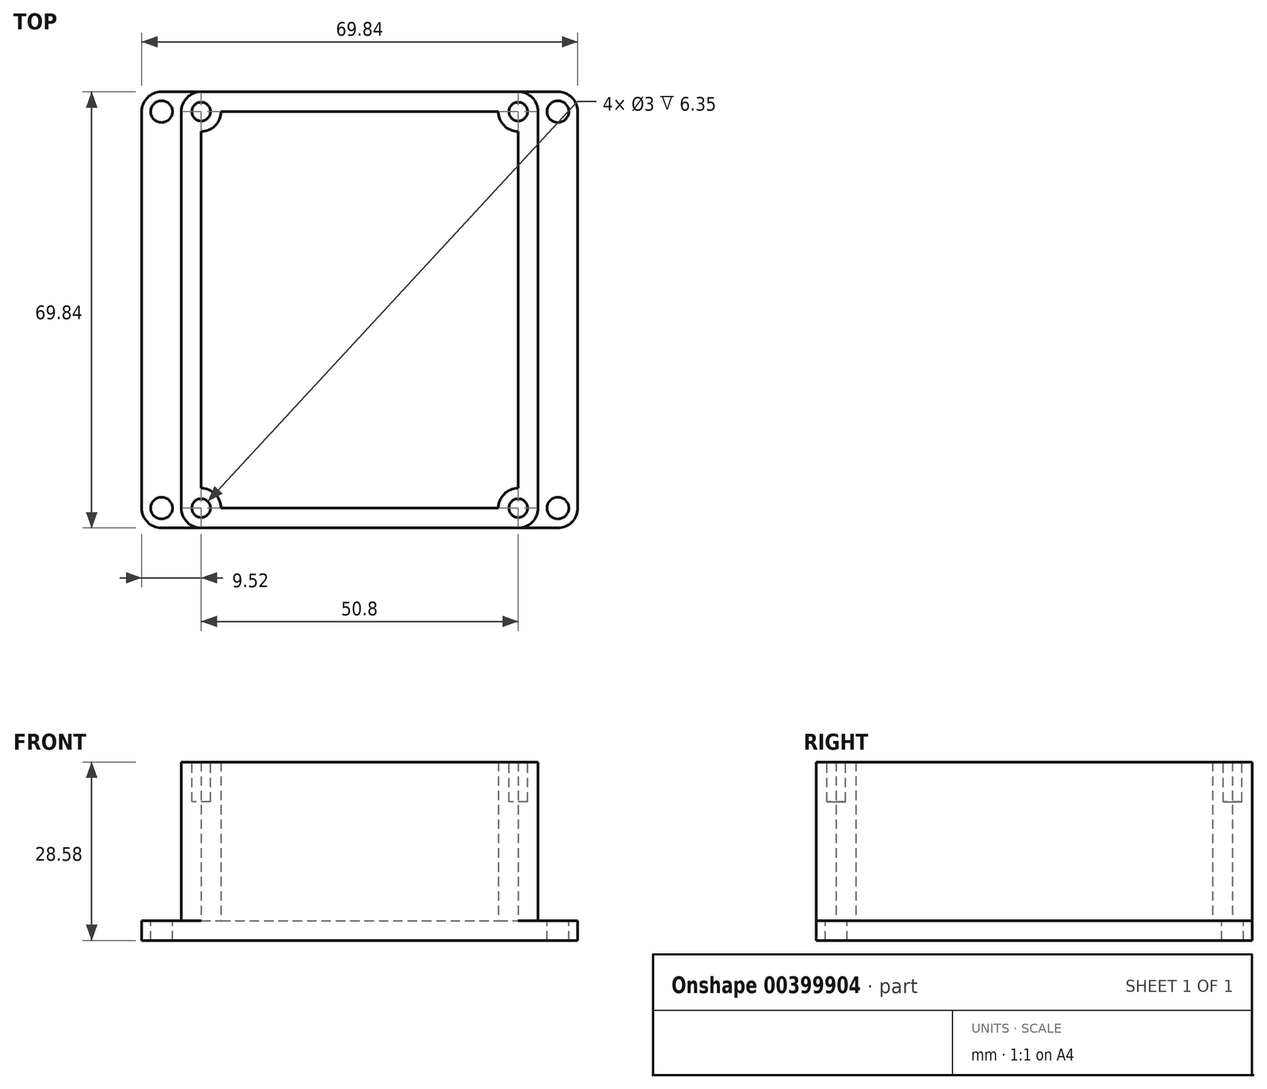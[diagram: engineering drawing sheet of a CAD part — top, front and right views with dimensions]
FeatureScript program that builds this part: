
annotation { "Feature Type Name" : "Feature", "Feature Type Description" : "" }
export const myFeature = defineFeature(function(context is Context, id is Id, definition is map)
    precondition{}
    {
        {
            var Q0;
            Q0=qCreatedBy(makeId("Top.planeOp"),FACE);
            var sketch = newSketch(context, id + "F0", { "sketchPlane" : qUnion([Q0])});
            skLineSegment(sketch, "E0.bottom", {"start": v(-34.93, 34.93) * mm, "end": v(34.93, 34.93) * mm});
            skLineSegment(sketch, "E0.top", {"start": v(-34.93, -34.93) * mm, "end": v(34.93, -34.93) * mm});
            skLineSegment(sketch, "E0.left", {"start": v(-34.93, 34.93) * mm, "end": v(-34.93, -34.93) * mm});
            skLineSegment(sketch, "E0.right", {"start": v(34.93, 34.93) * mm, "end": v(34.93, -34.93) * mm});
            skSolve(sketch);
        }
        {
            var Q0;
            Q0=qSketchRegion(id+"F0",true);
            extrude(context, id + "F1", {"entities" : qUnion([Q0]), "depth" : 3.17 * mm});
        }
        {
            var Q0;
            Q0=makeQuery(id+"F1.opExtrude","SWEPT_EDGE",EDGE,{"disambiguationData":[OSD([sQuery(id+"F0.wireOp",EDGE,"E0.top"),sQuery(id+"F0.wireOp",EDGE,"E0.left")])]});
            var Q1;
            Q1=makeQuery(id+"F1.opExtrude","SWEPT_EDGE",EDGE,{"disambiguationData":[OSD([sQuery(id+"F0.wireOp",EDGE,"E0.top"),sQuery(id+"F0.wireOp",EDGE,"E0.right")])]});
            var Q2;
            Q2=makeQuery(id+"F1.opExtrude","SWEPT_EDGE",EDGE,{"disambiguationData":[OSD([sQuery(id+"F0.wireOp",EDGE,"E0.bottom"),sQuery(id+"F0.wireOp",EDGE,"E0.right")])]});
            var Q3;
            Q3=makeQuery(id+"F1.opExtrude","SWEPT_EDGE",EDGE,{"disambiguationData":[OSD([sQuery(id+"F0.wireOp",EDGE,"E0.bottom"),sQuery(id+"F0.wireOp",EDGE,"E0.left")])]});
            fillet(context, id + "F2", {"entities" : qUnion([Q0, Q1, Q2, Q3]), "radius" : 3.17 * mm, "tangentPropagation" : true, "allowEdgeOverflow" : false});
        }
        {
            var Q0;
            Q0=makeQuery(id+"F1.opExtrude","CAP_FACE",FACE,{"disambiguationData":[OSD([sQuery(id+"F0.wireOp",EDGE,"E0.bottom"),sQuery(id+"F0.wireOp",EDGE,"E0.top"),sQuery(id+"F0.wireOp",EDGE,"E0.left"),sQuery(id+"F0.wireOp",EDGE,"E0.right")])],"isStart":false});
            var sketch = newSketch(context, id + "F3", { "sketchPlane" : qUnion([Q0])});
            skCircle(sketch, "E1", {"center": v(-31.75, 31.75) * mm, "radius": 1.75 * mm});
            skCircle(sketch, "E2", {"center": v(31.75, 31.75) * mm, "radius": 1.75 * mm});
            skCircle(sketch, "E3", {"center": v(31.75, -31.75) * mm, "radius": 1.75 * mm});
            skCircle(sketch, "E4", {"center": v(-31.75, -31.75) * mm, "radius": 1.75 * mm});
            skSolve(sketch);
        }
        {
            var Q0;
            Q0=qSketchRegion(id+"F3",true);
            extrude(context, id + "F4", {"entities" : qUnion([Q0]), "operationType" : NewBodyOperationType.REMOVE, "oppositeDirection" : true, "depth" : 25.4 * mm, "hasSecondDirection" : true, "secondDirectionBound" : SecondDirectionBoundingType.THROUGH_ALL, "secondDirectionOppositeDirection" : false, "secondDirectionDepth" : 25.4 * mm});
        }
        {
            var Q0;
            Q0=makeQuery(id+"F1.opExtrude","CAP_FACE",FACE,{"disambiguationData":[OSD([sQuery(id+"F0.wireOp",EDGE,"E0.bottom"),sQuery(id+"F0.wireOp",EDGE,"E0.top"),sQuery(id+"F0.wireOp",EDGE,"E0.left"),sQuery(id+"F0.wireOp",EDGE,"E0.right")])],"isStart":false});
            var sketch = newSketch(context, id + "F5", { "sketchPlane" : qUnion([Q0])});
            skLineSegment(sketch, "E5.bottom", {"start": v(-25.4, 34.93) * mm, "end": v(25.4, 34.93) * mm});
            skLineSegment(sketch, "E5.top", {"start": v(-25.4, -34.93) * mm, "end": v(25.4, -34.93) * mm});
            skLineSegment(sketch, "E5.left", {"start": v(-28.58, 31.75) * mm, "end": v(-28.58, -31.75) * mm});
            skLineSegment(sketch, "E5.right", {"start": v(28.57, 31.75) * mm, "end": v(28.58, -31.75) * mm});
            skLineSegment(sketch, "E6.bottom", {"start": v(-22.23, 31.75) * mm, "end": v(22.22, 31.75) * mm});
            skLineSegment(sketch, "E6.top", {"start": v(-22.23, -31.75) * mm, "end": v(22.23, -31.75) * mm});
            skLineSegment(sketch, "E6.left", {"start": v(-25.4, 28.57) * mm, "end": v(-25.4, -28.58) * mm});
            skLineSegment(sketch, "E6.right", {"start": v(25.4, 28.58) * mm, "end": v(25.4, -28.58) * mm});
            skPoint(sketch, "E7.visualSharp", {"position": v(-25.4, 31.75) * mm});
            skPoint(sketch, "E8.visualSharp", {"position": v(-28.58, 34.93) * mm});
            skPoint(sketch, "E9.visualSharp", {"position": v(-25.4, -31.75) * mm});
            skPoint(sketch, "E10.visualSharp", {"position": v(-28.58, -34.93) * mm});
            skPoint(sketch, "E11.visualSharp", {"position": v(28.58, -34.93) * mm});
            skPoint(sketch, "E12.visualSharp", {"position": v(25.4, -31.75) * mm});
            skPoint(sketch, "E13.visualSharp", {"position": v(25.4, 31.75) * mm});
            skPoint(sketch, "E14.visualSharp", {"position": v(28.57, 34.93) * mm});
            skArc(sketch, "E15", {"start": v(-25.4, 28.57) * mm, "mid": v(-23.15, 29.5) * mm, "end": v(-22.23, 31.75) * mm});
            skArc(sketch, "E16.trimOffspring", {"start": v(-25.4, 34.92) * mm, "mid": v(-27.65, 34) * mm, "end": v(-28.58, 31.75) * mm});
            skArc(sketch, "E17", {"start": v(22.22, 31.75) * mm, "mid": v(23.15, 29.5) * mm, "end": v(25.4, 28.58) * mm});
            skArc(sketch, "E18.trimOffspring", {"start": v(28.57, 31.75) * mm, "mid": v(27.65, 34) * mm, "end": v(25.4, 34.93) * mm});
            skArc(sketch, "E19", {"start": v(-28.58, -31.75) * mm, "mid": v(-27.65, -34) * mm, "end": v(-25.4, -34.93) * mm});
            skArc(sketch, "E20.trimOffspring", {"start": v(-22.23, -31.75) * mm, "mid": v(-23.15, -29.5) * mm, "end": v(-25.4, -28.58) * mm});
            skArc(sketch, "E21", {"start": v(25.4, -28.58) * mm, "mid": v(23.15, -29.5) * mm, "end": v(22.23, -31.75) * mm});
            skArc(sketch, "E22.trimOffspring", {"start": v(25.4, -34.93) * mm, "mid": v(27.65, -34) * mm, "end": v(28.58, -31.75) * mm});
            skSolve(sketch);
        }
        {
            var Q0;
            Q0=qSketchRegion(id+"F5",true);
            extrude(context, id + "F6", {"entities" : qUnion([Q0]), "operationType" : NewBodyOperationType.ADD, "depth" : 25.4 * mm});
        }
        {
            var Q0;
            Q0=makeQuery(id+"F6.opExtrude","CAP_FACE",FACE,{"disambiguationData":[OSD([sQuery(id+"F5.wireOp",EDGE,"E5.bottom"),sQuery(id+"F5.wireOp",EDGE,"E5.top"),sQuery(id+"F5.wireOp",EDGE,"E5.left"),sQuery(id+"F5.wireOp",EDGE,"E5.right"),sQuery(id+"F5.wireOp",EDGE,"E6.bottom"),sQuery(id+"F5.wireOp",EDGE,"E6.top"),sQuery(id+"F5.wireOp",EDGE,"E6.left"),sQuery(id+"F5.wireOp",EDGE,"E6.right"),sQuery(id+"F5.wireOp",EDGE,"E15"),sQuery(id+"F5.wireOp",EDGE,"E16.trimOffspring"),sQuery(id+"F5.wireOp",EDGE,"E17"),sQuery(id+"F5.wireOp",EDGE,"E18.trimOffspring"),sQuery(id+"F5.wireOp",EDGE,"E19"),sQuery(id+"F5.wireOp",EDGE,"E20.trimOffspring"),sQuery(id+"F5.wireOp",EDGE,"E21"),sQuery(id+"F5.wireOp",EDGE,"E22.trimOffspring")])],"isStart":false});
            var sketch = newSketch(context, id + "F7", { "sketchPlane" : qUnion([Q0])});
            skCircle(sketch, "E23", {"center": v(-25.4, 31.75) * mm, "radius": 1.5 * mm});
            skCircle(sketch, "E24", {"center": v(25.4, 31.75) * mm, "radius": 1.5 * mm});
            skCircle(sketch, "E25", {"center": v(25.4, -31.75) * mm, "radius": 1.5 * mm});
            skCircle(sketch, "E26", {"center": v(-25.4, -31.75) * mm, "radius": 1.5 * mm});
            skSolve(sketch);
        }
        {
            var Q0;
            Q0=qSketchRegion(id+"F7",true);
            extrude(context, id + "F8", {"entities" : qUnion([Q0]), "operationType" : NewBodyOperationType.REMOVE, "oppositeDirection" : true, "depth" : 6.35 * mm});
        }
        {
            var Q0;
            Q0=makeQuery(id+"F6.boolean.opBoolean","SPLIT",FACE,{"disambiguationData":[TD([makeQuery(id+"F6.opExtrude","SWEPT_FACE",FACE,{"disambiguationData":[OSD([sQuery(id+"F5.wireOp",EDGE,"E6.bottom")])]})])],"derivedFrom":makeQuery(id+"F1.opExtrude","CAP_FACE",FACE,{"disambiguationData":[OSD([sQuery(id+"F0.wireOp",EDGE,"E0.bottom"),sQuery(id+"F0.wireOp",EDGE,"E0.top"),sQuery(id+"F0.wireOp",EDGE,"E0.left"),sQuery(id+"F0.wireOp",EDGE,"E0.right")])],"isStart":false})});
            cPlane(context, id + "F9", {"entities" : qUnion([Q0]), "cplaneType" : CPlaneType.OFFSET, "offset" : 3.17 * mm, "width" : 152.4 * mm, "height" : 152.4 * mm});
        }
        {
            var Q0;
            Q0=qCreatedBy(id+"F9.planeOp",FACE);
            var sketch = newSketch(context, id + "F10", { "sketchPlane" : qUnion([Q0])});
            skLineSegment(sketch, "E27.bottom", {"start": v(-21.92, 28.61) * mm, "end": v(22.53, 28.61) * mm});
            skLineSegment(sketch, "E27.top", {"start": v(-21.92, -28.54) * mm, "end": v(22.53, -28.54) * mm});
            skLineSegment(sketch, "E27.left", {"start": v(-21.92, 28.61) * mm, "end": v(-21.92, -28.54) * mm});
            skLineSegment(sketch, "E27.right", {"start": v(22.53, 28.61) * mm, "end": v(22.53, -28.54) * mm});
            skSolve(sketch);
        }
        {
            var Q0;
            Q0=qSketchRegion(id+"F10",true);
            extrude(context, id + "F11", {"entities" : qUnion([Q0]), "depth" : 1.27 * mm});
        }
        {
            var Q0;
            Q0=makeQuery(id+"F11.opExtrude","CAP_FACE",FACE,{"disambiguationData":[OSD([sQuery(id+"F10.wireOp",EDGE,"E27.bottom"),sQuery(id+"F10.wireOp",EDGE,"E27.top"),sQuery(id+"F10.wireOp",EDGE,"E27.left"),sQuery(id+"F10.wireOp",EDGE,"E27.right")])],"isStart":false});
            var sketch = newSketch(context, id + "F12", { "sketchPlane" : qUnion([Q0])});
            skLineSegment(sketch, "E28.bottom", {"start": v(-17.3, -28.54) * mm, "end": v(-8.3, -28.54) * mm});
            skLineSegment(sketch, "E28.top", {"start": v(-17.3, -14.13) * mm, "end": v(-8.3, -14.13) * mm});
            skLineSegment(sketch, "E28.left", {"start": v(-17.3, -28.54) * mm, "end": v(-17.3, -14.13) * mm});
            skLineSegment(sketch, "E28.right", {"start": v(-8.3, -28.54) * mm, "end": v(-8.3, -14.13) * mm});
            skSolve(sketch);
        }
        {
            var Q0;
            Q0=qSketchRegion(id+"F12",true);
            extrude(context, id + "F13", {"entities" : qUnion([Q0]), "operationType" : NewBodyOperationType.ADD, "depth" : 11 * mm});
        }
        {
            var Q0;
            Q0=makeQuery(id+"F11.opExtrude","SWEPT_BODY",BODY,{"disambiguationData":[OSD([sQuery(id+"F10.wireOp",EDGE,"E27.bottom"),sQuery(id+"F10.wireOp",EDGE,"E27.top"),sQuery(id+"F10.wireOp",EDGE,"E27.left"),sQuery(id+"F10.wireOp",EDGE,"E27.right")])]});
            deleteBodies(context, id + "F14", {"entities" : qUnion([Q0])});
        }
    });
